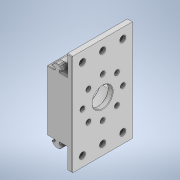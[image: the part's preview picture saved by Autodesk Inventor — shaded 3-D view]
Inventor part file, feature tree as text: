
AUTODESK INVENTOR PART (.ipt)
format: ipt  version: 2020 (Build 240168000, 168)  size: 599,040 bytes
history: native  units: in
note: dims shown in document units (in); Inventor stores cm internally (conversion verified against a paired STEP export)
features: reference x24, sketch x8, extrude x7, other x4, chamfer x3, fillet x2, projected_geometry x1
ambient origin geometry x8: Origin, YZ Plane, XZ Plane, XY Plane, X Axis, Y Axis, Z Axis, Center Point
bodies: Solid1 (feature_tree)
feature tree (49):
  extrude  "Extrusion1"  Depth=5.0in
  extrude  "Extrusion2"  Depth=3.0in TaperAngle=0.0deg
  extrude  "Extrusion3"  Depth=0.5in
  chamfer  "Chamfer1"  Distance=1.0in
  extrude  "Extrusion4"  Depth=0.125in TaperAngle=360.0deg
  sketch  "Sketch6"  dims[d8=0.7874in d10=4.0in d11=1.1811in d13=1.0in]
  fillet  "Fillet1"  [1 undecoded]
  chamfer  "Chamfer2"  Distance=2.6in
  extrude  "Extrusion6"  Depth=0.125in TaperAngle=0.0deg
  extrude  "Extrusion7"  Depth=0.125in TaperAngle=45.0deg
  extrude  "Extrusion8"  Depth=0.125in
  fillet  "Fillet2"  Radius=1.396in
  chamfer  "Chamfer4"  Distance=0.2in
  sketch  "Sketch1"  dims[d0=1.25in d1=5.0in]
  reference  "Reference1"
  reference  "Reference2"
  reference  "Reference3"
  reference  "Reference4"
  reference  "Reference5"
  reference  "Reference6"
  reference  "Reference7"
  reference  "Reference8"
  reference  "Reference9"
  reference  "Reference10"
  reference  "Reference11"
  reference  "Reference12"
  reference  "Reference13"
  reference  "Reference14"
  reference  "Reference15"
  reference  "Reference16"
  reference  "Reference17"
  reference  "Reference18"
  reference  "Reference19"
  reference  "Reference20"
  reference  "Reference21"
  reference  "Reference22"
  reference  "Reference23"
  reference  "Reference24"
  sketch  "Sketch2"  dims[d2=0.25in d3=3.0in d4=0.0in]
  sketch  "Sketch3"  dims[d5=0.5in d6=0.5in]
  sketch  "Sketch5"  dims[d7=0.2656in]
  sketch  "Sketch9"  dims[d16=1.0in]
  sketch  "Sketch10"  dims[d17=2.5in]
  sketch  "Sketch11"  dims[d18=0.2031in d19=1.0in d20=3.1496in d22=360.0deg d24=0.0in d25=0.0in d26=2.6in d27=1.0in d28=0.0in d29=0.025in d30=0.125in d31=45.0deg d33=1.396in d34=1.396in d35=0.2in d36=0.7874in d38=1.396in d39=0.7874in d41=1.396in d44=0.0in d45=0.0in d46=1.75in d47=1.75in d48=0.0098in d49=0.0098in d50=0.025in d51=0.02in d52=0.125in d53=45.0deg d56=1.1811in d58=1.0in d59=0.7874in d61=4.0in d64=0.125in d65=0.0in d66=0.7874in d68=4.0in d69=1.1811in d71=1.0in d74=0.6in d75=0.0in d76=0.0in d77=1.25in d78=0.25in d79=1.0in d80=0.0in d84=0.125in d85=0.025in d86=0.125in d87=45.0deg]
  projected_geometry  "Projected Loop1"
  other  "<userpath>\Documents\FRC\2020\ShooterPrototype.iam"
  other  "ShooterPrototype.iam"
  other  "9inSpacer:1"
  other  "1003-48-CL:4"
note: 1 required parameter value undecoded (feature->parameter linkage not recoverable at this tier; creation-order binding heuristic only, values carry confidence <= 0.55)
